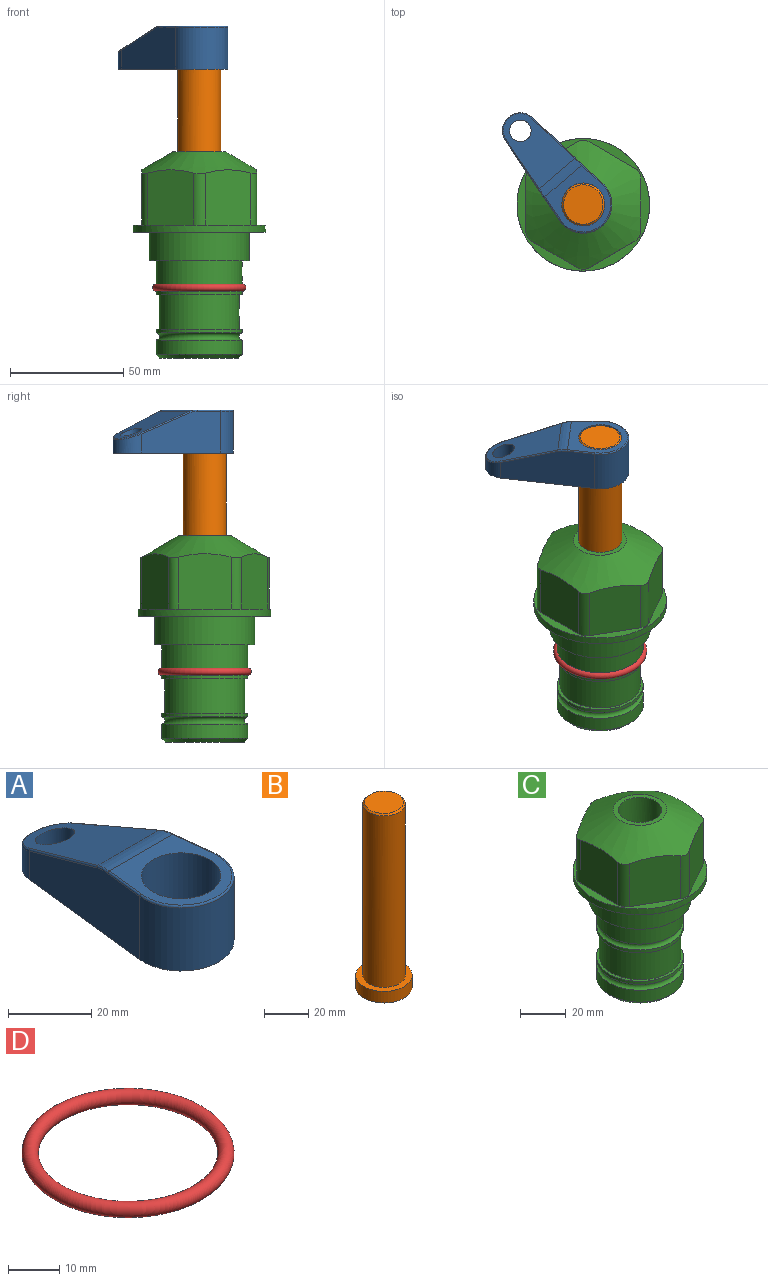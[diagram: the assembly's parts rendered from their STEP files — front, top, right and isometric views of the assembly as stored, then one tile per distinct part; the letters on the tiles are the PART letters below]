
ASSEMBLY  parts=4 mates=2
PART A: 44 faces, bbox 27.5x64.5x19.1 mm
  f0: plane 2.3x0.95mm, normal (0,0,-1), area 1mm2, adj f25,f30,f34
  f1: plane 63.5x25.4mm, normal (0,0,-1), area 561.7mm2, adj f2,f3,f4,f5,f6,f7,f19,f20
  f2: cylinder r=12.7mm len=25.4mm, axis (0,0,-1), area 792.2mm2, adj f1,f3,f5,f13
  f3: plane 42.33x18.54mm, normal (0.99,0.11,0), area 647mm2, adj f1,f2,f4,f11,f12,f14
  f4: cylinder r=7.94mm len=15.78mm, axis (0,0,-1), area 158.6mm2, adj f1,f3,f5,f16
  f5: plane 42.33x18.54mm, normal (-0.99,0.11,0), area 647mm2, adj f1,f2,f4,f15,f17,f18
  f6: cylinder r=9.53mm len=19.05mm, axis (0,0,-1), area 1140.1mm2, adj f1,f8
  f7: cylinder r=4.76mm len=10.98mm, axis (0,0,-1), area 276.1mm2, adj f1,f9
  f8: plane 25.83x24.38mm, normal (0,0,1), area 262.2mm2, adj f6,f10,f11,f13,f15
  f9: plane 32.49x20.55mm, normal (0,0.34,0.94), area 489.9mm2, adj f7,f10,f14,f16,f18
  f10: cylinder r=12.7mm len=21.49mm, axis (-1,0,0), area 93.2mm2, adj f8,f9,f12,f17
  f11: cylinder r=0.51mm len=12.34mm, axis (0.11,-0.99,0), area 9.9mm2, adj f3,f8,f12,f13
  f12: bspline ~7.62x1.64mm, area 3.5mm2, adj f3,f10,f11,f14
  f13: torus R=12.19mm, axis (0,0,1), area 33.6mm2, adj f2,f8,f11,f15
  f14: cylinder r=0.51mm len=26.01mm, axis (0.1,-0.93,0.34), area 21.6mm2, adj f3,f9,f12,f16
  f15: cylinder r=0.51mm len=12.34mm, axis (0.11,0.99,0), area 9.9mm2, adj f5,f8,f13,f17
  f16: bspline ~15.78x7.05mm, area 15.7mm2, adj f4,f9,f14,f18
  f17: bspline ~7.62x1.64mm, area 3.5mm2, adj f5,f10,f15,f18
  f18: cylinder r=0.51mm len=26.01mm, axis (0.1,0.93,-0.34), area 21.6mm2, adj f5,f9,f16,f17
  f19: plane 21.6x14.29mm, normal (-0.99,-0.11,0), area 242.6mm2, adj f1,f26,f28,f34,f36,f38
  f20: plane 21.6x14.29mm, normal (0.99,-0.11,0), area 242.6mm2, adj f1,f27,f29,f37,f39,f41
  f21: cylinder r=12.7mm len=14.29mm, axis (0,0,-1), area 173.2mm2, adj f1,f26,f27,f30,f31,f33
  f22: cylinder r=7.94mm len=7.63mm, axis (0,0,-1), area 53.8mm2, adj f1,f28,f29,f42
  f23: plane 2.3x0.95mm, normal (0,0,-1), area 1mm2, adj f25,f33,f37
  f24: plane 17.94x12.32mm, normal (0,-0.34,-0.94), area 191.2mm2, adj f25,f38,f41,f42
  f25: cylinder r=9.53mm len=12.93mm, axis (-1,0,0), area 37.5mm2, adj f0,f23,f24,f31,f36,f39
  f26: cylinder r=1.59mm len=14.29mm, axis (0,0,-1), area 49mm2, adj f1,f19,f21,f32
  f27: cylinder r=1.59mm len=14.29mm, axis (0,0,-1), area 49mm2, adj f1,f20,f21,f35
  f28: cylinder r=1.59mm len=7.28mm, axis (0,0,-1), area 22.1mm2, adj f1,f19,f22,f40
  f29: cylinder r=1.59mm len=7.28mm, axis (0,0,-1), area 22.1mm2, adj f1,f20,f22,f43
  f30: torus R=14.29mm, axis (0,0,1), area 5.8mm2, adj f0,f21,f31,f32
  f31: bspline ~11.06x2.73mm, area 20.8mm2, adj f21,f25,f30,f33
  f32: sphere r=1.59mm, area 5.4mm2, adj f26,f30,f34
  f33: torus R=14.29mm, axis (0,0,1), area 5.8mm2, adj f21,f23,f31,f35
  f34: cylinder r=1.59mm len=1.68mm, axis (-0.11,0.99,0), area 2.4mm2, adj f0,f19,f32,f36
  f35: sphere r=1.59mm, area 5.4mm2, adj f27,f33,f37
  f36: bspline ~5.82x2.33mm, area 7.7mm2, adj f19,f25,f34,f38
  f37: cylinder r=1.59mm len=1.68mm, axis (0.11,0.99,0), area 2.4mm2, adj f20,f23,f35,f39
  f38: cylinder r=1.59mm len=18.33mm, axis (0.1,-0.93,0.34), area 46.7mm2, adj f19,f24,f36,f40
  f39: bspline ~5.82x2.33mm, area 7.7mm2, adj f20,f25,f37,f41
  f40: sphere r=1.59mm, area 3.6mm2, adj f28,f38,f42
  f41: cylinder r=1.59mm len=18.33mm, axis (0.1,0.93,-0.34), area 46.7mm2, adj f20,f24,f39,f43
  f42: bspline ~8.31x1.84mm, area 15.3mm2, adj f22,f24,f40,f43
  f43: sphere r=1.59mm, area 3.6mm2, adj f29,f41,f42
PART B: 6 faces, bbox 25.4x25.4x101.6 mm
  f0: plane 17.46x17.46mm, normal (0,0,1), area 239.5mm2, adj f5
  f1: plane 25.4x25.4mm, normal (0,0,-1), area 506.7mm2, adj f2
  f2: cylinder r=12.7mm len=25.4mm, axis (0,0,1), area 506.7mm2, adj f1,f3
  f3: plane 25.4x25.4mm, normal (0,0,1), area 221.7mm2, adj f2,f4
  f4: cylinder r=9.53mm len=94.46mm, axis (0,0,1), area 5653mm2, adj f3,f5
  f5: cone r=8.73mm half-angle=45deg, axis (0,0,-1), area 64.4mm2, adj f0,f4
PART C: 36 faces, bbox 58.7x58.7x91.2 mm
  f0: cylinder r=17.78mm len=35.56mm, axis (0,0,1), area 1670.8mm2, adj f23,f24,f31
  f1: cylinder r=19.05mm len=38.1mm, axis (0,0,1), area 1191.9mm2, adj f26,f27,f30
  f2: plane 58.66x58.66mm, normal (0,0,-1), area 1150.6mm2, adj f3,f28
  f3: cylinder r=29.33mm len=58.66mm, axis (0,0,-1), area 585.1mm2, adj f2,f4
  f4: plane 58.66x58.66mm, normal (0,0,1), area 475.9mm2, adj f3,f5,f6,f7,f8,f9,f10,f11
  f5: plane 24.5x20.32mm, normal (-0.5,0.87,0), area 562.8mm2, adj f4,f15,f16,f17
  f6: plane 24.5x20.32mm, normal (0.5,0.87,0), area 562.8mm2, adj f4,f14,f15,f17
  f7: plane 24.5x23.48mm, normal (1,0,0), area 562.8mm2, adj f4,f13,f14,f17
  f8: plane 24.5x20.32mm, normal (0.5,-0.87,0), area 562.8mm2, adj f4,f12,f13,f17
  f9: plane 24.5x20.32mm, normal (-0.5,-0.87,0), area 562.8mm2, adj f4,f11,f12,f17
  f10: plane 24.5x23.48mm, normal (-1,0,0), area 562.8mm2, adj f4,f11,f16,f17
  f11: cylinder r=5.08mm len=23.01mm, axis (0,0,-1), area 121.2mm2, adj f4,f9,f10,f17
  f12: cylinder r=5.08mm len=23.01mm, axis (0,0,-1), area 121.2mm2, adj f4,f8,f9,f17
  f13: cylinder r=5.08mm len=23.01mm, axis (0,0,-1), area 121.2mm2, adj f4,f7,f8,f17
  f14: cylinder r=5.08mm len=23.01mm, axis (0,0,-1), area 121.2mm2, adj f4,f6,f7,f17
  f15: cylinder r=5.08mm len=23.01mm, axis (0,0,-1), area 121.2mm2, adj f4,f5,f6,f17
  f16: cylinder r=5.08mm len=23.01mm, axis (0,0,-1), area 121.2mm2, adj f4,f5,f10,f17
  f17: cone r=11.73mm half-angle=60deg, axis (0,0,-1), area 2071.8mm2, adj f5,f6,f7,f8,f9,f10,f11,f12
  f18: plane 23.46x23.46mm, normal (0,0,1), area 147.4mm2, adj f17,f35
  f19: plane 34.93x34.93mm, normal (0,0,-1), area 958mm2, adj f29
  f20: cylinder r=19.05mm len=38.1mm, axis (0,0,1), area 760.1mm2, adj f21,f29
  f21: torus R=19.05mm, axis (0,0,1), area 565.3mm2, adj f20,f22
  f22: cylinder r=19.05mm len=38.1mm, axis (0,0,1), area 190mm2, adj f21,f23
  f23: plane 38.1x38.1mm, normal (0,0,1), area 146.9mm2, adj f0,f22
  f24: plane 38.1x38.1mm, normal (0,0,-1), area 146.9mm2, adj f0,f25
  f25: cylinder r=19.05mm len=38.1mm, axis (0,0,1), area 190mm2, adj f24,f26
  f26: torus R=19.05mm, axis (0,0,1), area 565.3mm2, adj f1,f25
  f27: plane 44.45x44.45mm, normal (0,0,-1), area 411.7mm2, adj f1,f28
  f28: cylinder r=22.23mm len=44.45mm, axis (0,0,1), area 1773.5mm2, adj f2,f27
  f29: cone r=19.05mm half-angle=45deg, axis (0,0,1), area 257.5mm2, adj f19,f20
  f30: cylinder r=3.17mm len=6.75mm, axis (-1,0,0), area 128mm2, adj f1,f33
  f31: cylinder r=3.17mm len=6.35mm, axis (-1,0,0), area 102.5mm2, adj f0,f33
  f32: plane 25.4x25.4mm, normal (0,0,1), area 506.7mm2, adj f33
  f33: cylinder r=12.7mm len=66.42mm, axis (0,0,-1), area 5236.2mm2, adj f30,f31,f32,f34
  f34: cone r=9.53mm half-angle=30deg, axis (0,0,-1), area 443.4mm2, adj f33,f35
  f35: cylinder r=9.53mm len=19.05mm, axis (0,0,-1), area 849mm2, adj f18,f34
PART D: 1 faces, bbox 44.7x44.7x3.2 mm
  f0: torus R=19.05mm, axis (0,0,1), area 1193.9mm2
PLACE A rot(axis=(0,0,1),40.5deg) t=(0,0,72.22)mm
PLACE B rot(axis=(0,0,1),40.5deg) t=(0,0,17.61)mm
PLACE C at identity fixed
PLACE D at identity
MATE cylindrical B.f2 <-> C.f0  axis (0,0,1) through (0,0,43.25)mm
MATE fastened A.f2 <-> B.f2  axis (0,0,-1) through (0,0,91.27)mm
